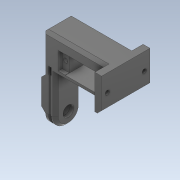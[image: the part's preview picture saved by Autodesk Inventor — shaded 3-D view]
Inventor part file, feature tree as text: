
AUTODESK INVENTOR PART (.ipt)
format: ipt  version: 2020 (Build 240168000, 168)  size: 900,096 bytes
history: native  units: mm
features: extrude x39, sketch x38, projected_geometry x26, chamfer x8, reference x8, other x5, plane x1, hole x1
ambient origin geometry x8: Origin, YZ Plane, XZ Plane, XY Plane, X Axis, Y Axis, Z Axis, Center Point
bodies: Solid1 (feature_tree)
feature tree (126):
  extrude  "Extrusion1"  Depth=45.0mm
  plane  "Work Plane1"
  extrude  "Extrusion2"  Depth=18.0mm
  extrude  "Extrusion3"  Depth=51.1mm TaperAngle=0.0deg
  extrude  "Extrusion4"  TaperAngle=0.0deg  [1 undecoded]
  extrude  "Extrusion5"  Depth=50.1mm TaperAngle=0.0deg
  sketch  "Sketch6"  dims[d14=7.199887mm d15=3.599976mm]
  extrude  "Extrusion6"  Depth=3.599976mm
  extrude  "Extrusion7"  Depth=0.15mm
  extrude  "Extrusion8"  Depth=0.15mm
  extrude  "Extrusion10"  Depth=15.9mm TaperAngle=0.0deg
  extrude  "Extrusion11"  Depth=23.15mm
  extrude  "Extrusion12"  Depth=3.925mm
  extrude  "Extrusion13"  Depth=5.15mm
  sketch  "Sketch14"  dims[d29=2.525mm d30=5.15mm]
  extrude  "Extrusion14"  Depth=12.55mm
  extrude  "Extrusion15"  Depth=2.75mm TaperAngle=0.0deg
  hole  "Hole1"  [1 undecoded]
  extrude  "Extrusion16"  Depth=2.525mm
  extrude  "Extrusion18"  Depth=23.15mm
  extrude  "Extrusion20"  Depth=10.0mm
  extrude  "Extrusion21"  Depth=0.0mm
  extrude  "Extrusion22"  TaperAngle=0.0deg  [1 undecoded]
  chamfer  "Chamfer1"  Distance=12.55mm
  chamfer  "Chamfer2"  Distance=4.0mm
  extrude  "Extrusion25"  Depth=3.85mm
  extrude  "Extrusion26"  Depth=0.765mm
  extrude  "Extrusion28"  Depth=18.0mm
  extrude  "Extrusion31"  Depth=5.0mm
  extrude  "Extrusion32"  Depth=53.1mm TaperAngle=0.0deg
  extrude  "Extrusion35"  Depth=10.0mm
  extrude  "Extrusion36"  Depth=10.0mm TaperAngle=0.0deg
  extrude  "Extrusion37"  Depth=10.0mm
  extrude  "Extrusion38"  Depth=10.0mm TaperAngle=0.0deg
  extrude  "Extrusion40"  Depth=10.0mm
  extrude  "Extrusion41"  Depth=10.0mm
  extrude  "Extrusion42"  Depth=10.0mm
  chamfer  "Chamfer5"  Distance=26.0mm
  extrude  "Extrusion43"  Depth=10.0mm
  extrude  "Extrusion44"  Depth=10.0mm
  chamfer  "Chamfer6"  Distance=4.0mm
  chamfer  "Chamfer7"  Distance=12.0mm
  extrude  "Extrusion45"  Depth=10.0mm TaperAngle=0.0deg
  extrude  "Extrusion46"  Depth=10.0mm TaperAngle=0.0deg
  extrude  "Extrusion47"  Depth=10.0mm
  chamfer  "Chamfer8"  Distance=15.292019mm
  chamfer  "Chamfer9"  Distance=67.65mm
  chamfer  "Chamfer11"  Distance=3.0mm Angle=45.0deg
  extrude  "Extrusion48"  Depth=10.0mm TaperAngle=45.0deg
  extrude  "Extrusion49"  Depth=10.0mm
  extrude  "Extrusion50"  Depth=10.0mm TaperAngle=0.0deg
  sketch  "Sketch1"  dims[d0=18.0mm d1=45.0mm]
  reference  "Reference1"
  sketch  "Sketch2"  dims[d2=45.0mm d3=18.0mm]
  reference  "Reference2"
  sketch  "Sketch3"  dims[d4=18.0mm d5=51.1mm d6=2.0mm d7=0.0mm d8=0.0mm]
  reference  "Reference3"
  reference  "Reference4"
  reference  "Reference5"
  reference  "Reference6"
  reference  "Reference7"
  reference  "Reference8"
  sketch  "Sketch4"  dims[d9=37.3mm d10=0.0mm]
  sketch  "Sketch5"  dims[d11=35.0mm d12=50.1mm d13=0.0mm]
  sketch  "Sketch8"  dims[d16=0.15mm d17=0.15mm]
  sketch  "Sketch10"  dims[d18=0.15mm d19=0.15mm]
  sketch  "Sketch11"  dims[d20=5.4mm d21=0.0mm d22=15.9mm d23=0.0mm]
  sketch  "Sketch12"  dims[d24=6.5mm d25=0.0mm d26=23.15mm]
  sketch  "Sketch13"  dims[d27=12.55mm d28=3.925mm]
  sketch  "Sketch15"  dims[d31=5.15mm d32=12.55mm]
  sketch  "Sketch17"  dims[d33=40.75mm d34=0.0mm d35=2.75mm d36=0.0mm]
  sketch  "Sketch19"  dims[d43=11.85mm d44=23.15mm]
  projected_geometry  "Projected Loop1"
  sketch  "Sketch21"  dims[d45=3.925mm d46=2.525mm]
  projected_geometry  "Projected Loop3"
  sketch  "Sketch22"  dims[d47=12.55mm d48=23.15mm]
  sketch  "Sketch23"  dims[d49=10.05mm d50=0.0mm d54=10.0mm]
  projected_geometry  "Projected Loop4"
  projected_geometry  "Projected Loop5"
  projected_geometry  "Projected Loop6"
  projected_geometry  "Projected Loop7"
  sketch  "Sketch26"  dims[d55=0.0mm d56=0.0mm]
  projected_geometry  "Projected Loop13"
  sketch  "Sketch27"  dims[d57=19.0mm d58=0.0mm]
  projected_geometry  "Projected Loop14"
  sketch  "Sketch29"  dims[d59=8.8mm]
  projected_geometry  "Projected Loop16"
  sketch  "Sketch32"  dims[d60=5.925mm]
  projected_geometry  "Projected Loop19"
  sketch  "Sketch33"  dims[d61=2.525mm]
  projected_geometry  "Projected Loop20"
  sketch  "Sketch36"  dims[d62=23.15mm]
  projected_geometry  "Projected Loop23"
  sketch  "Sketch37"  dims[d63=15.075mm]
  projected_geometry  "Projected Loop24"
  sketch  "Sketch38"  dims[d64=23.15mm]
  projected_geometry  "Projected Loop25"
  sketch  "Sketch39"  dims[d65=6.05mm]
  projected_geometry  "Projected Loop26"
  sketch  "Sketch41"  dims[d66=23.15mm d67=12.55mm d68=0.0mm]
  projected_geometry  "Projected Loop28"
  sketch  "Sketch42"  dims[d72=8.8mm]
  projected_geometry  "Projected Loop29"
  sketch  "Sketch43"  dims[d73=10.0mm]
  projected_geometry  "Projected Loop30"
  projected_geometry  "Projected Loop31"
  sketch  "Sketch44"  dims[d74=10.2mm]
  sketch  "Sketch45"  dims[d75=17.225mm d76=4.0mm d77=0.0mm]
  projected_geometry  "Projected Loop32"
  projected_geometry  "Projected Loop33"
  projected_geometry  "Projected Loop34"
  sketch  "Sketch46"  dims[d78=3.85mm d79=10.925mm]
  projected_geometry  "Projected Loop35"
  sketch  "Sketch47"  dims[d80=5.0mm d81=0.0mm d82=0.765mm]
  projected_geometry  "Projected Loop36"
  sketch  "Sketch48"  dims[d83=2.7mm d84=0.0mm d85=18.0mm]
  projected_geometry  "Projected Loop37"
  sketch  "Sketch49"  dims[d86=5.0mm d87=5.0mm]
  sketch  "Sketch50"  dims[d88=53.1mm d89=0.0mm d90=53.1mm d91=0.0mm]
  projected_geometry  "Projected Loop38"
  sketch  "Sketch51"  dims[d92=3.0mm d93=6.0mm d94=4.0mm d95=2.0mm d96=90.0deg d97=40.0mm d98=0.0mm d99=3.1mm d100=2.4mm d101=0.0mm d105=3.1mm d106=2.4mm d107=0.0mm d112=8.0mm d113=24.0mm d114=3.0mm d115=26.0mm d116=3.0mm d117=4.0mm d118=4.0mm d119=12.0mm d120=10.0mm d121=0.0mm d124=2.4mm d125=0.0mm d126=37.142391mm d127=15.292019mm d128=67.65mm d129=0.0mm d130=3.0mm d131=2.0mm d132=45.0deg d197=2.0mm d198=2.0mm d199=45.0deg d200=7.0mm d201=7.0mm d202=0.0mm d203=6.0mm d204=0.0mm d211=5.0mm d212=0.0mm d225=7.0mm d226=3.0mm d227=19.5mm d228=0.0mm d229=7.0mm d230=2.0mm d231=0.0mm d238=36.05mm d239=30.324982mm d240=68.0mm d241=0.0mm d242=7.0mm d243=7.0mm d244=10.0mm d245=0.0mm d246=10.0mm d247=0.0mm d248=2.5mm d249=1.0mm d250=1.0mm d251=10.0mm d252=0.0mm d255=27.0mm d256=1.0mm d257=2.0mm d258=2.5mm d259=0.0mm d260=27.0mm d261=1.0mm d262=2.0mm d263=90.0deg d264=90.0deg d265=2.5mm d266=0.0mm d270=9.0mm d271=0.0mm d272=2.5mm d273=2.0mm d274=45.0deg d275=2.5mm d276=2.0mm d277=0.0mm d278=2.0mm d279=1.0mm d280=4.0mm d281=0.5mm d282=90.0deg d283=0.5mm d284=2.0mm d285=0.0mm d286=2.0mm d287=2.0mm d288=45.0deg d289=2.0mm d290=2.0mm d291=45.0deg d292=5.0mm d293=20.0mm d294=0.5mm d295=0.5mm d296=90.0deg d297=1.0mm d298=0.0mm d299=5.0mm d300=0.5mm d301=90.0deg d302=0.5mm d303=90.0deg d304=1.0mm d305=0.0mm d306=3.0mm d307=20.475036mm d308=7.0mm d309=0.0mm d310=7.0mm d311=2.0mm d312=45.0deg d313=1.0mm d314=2.0mm d315=45.0deg d319=2.0mm d320=2.0mm d321=45.0deg d322=0.15mm d323=0.15mm d324=0.15mm d325=0.15mm d326=10.0mm d327=0.0mm d328=0.1mm d329=0.1mm d330=10.0mm d331=0.0mm d332=10.8mm d333=0.0mm d108=0.5mm d109=0.872665mm d148=0.5mm d149=0.872665mm d150=0.5mm d151=0.872665mm d334=0.5mm d335=0.872665mm]
  parser-record x1  (decoder bookkeeping rows leaked as tree rows — omitted from the tree; the rows remain in map.json)
  other  "Demo2.0004.iam"
  other  "Bearing:2"
  other  "Rolling bearing GB/T 7218-1995 Type FSN 70000-Z F 623-Z:1"
  other  "servo horn 1:1"
note: 3 required parameter values undecoded (feature->parameter linkage not recoverable at this tier; creation-order binding heuristic only, values carry confidence <= 0.55)
note: 1 file-system path scrubbed to <path> (originals preserved in map.json)
